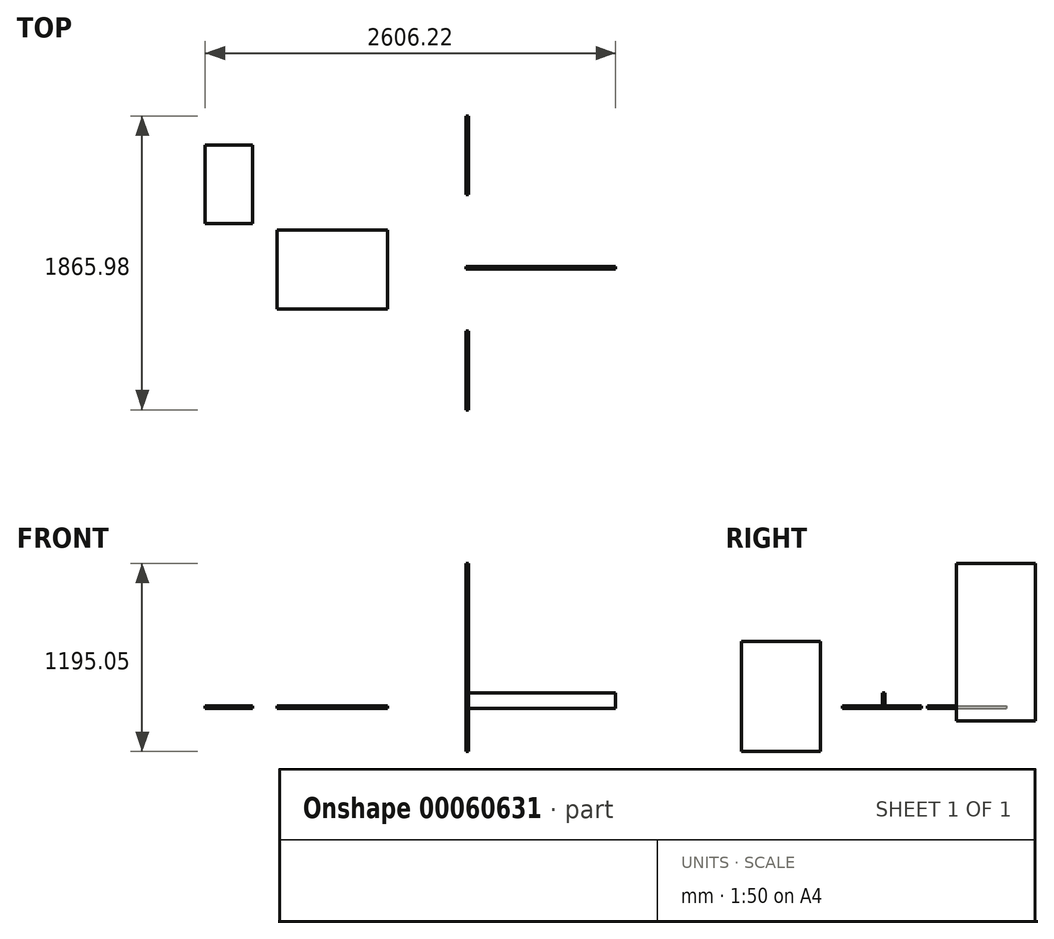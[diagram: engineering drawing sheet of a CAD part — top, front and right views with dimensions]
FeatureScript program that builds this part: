
annotation { "Feature Type Name" : "Feature", "Feature Type Description" : "" }
export const myFeature = defineFeature(function(context is Context, id is Id, definition is map)
    precondition{}
    {
        {
            var Q0;
            Q0=qCreatedBy(makeId("Front.planeOp"),FACE);
            var sketch = newSketch(context, id + "F0", { "sketchPlane" : qUnion([Q0])});
            skLineSegment(sketch, "E0.bottom", {"start": v(0, 100) * mm, "end": v(950, 100) * mm});
            skLineSegment(sketch, "E0.top", {"start": v(0, 0) * mm, "end": v(950, 0) * mm});
            skLineSegment(sketch, "E0.left", {"start": v(0, 100) * mm, "end": v(0, 0) * mm});
            skLineSegment(sketch, "E0.right", {"start": v(950, 100) * mm, "end": v(950, 0) * mm});
            skSolve(sketch);
        }
        {
            var Q0;
            Q0 = qSketchRegion(id + "F0", true);
            extrude(context, id + "F1", {"entities" : qUnion([Q0]), "depth" : 16 * mm});
        }
        {
            var Q0;
            Q0=qCreatedBy(makeId("Right.planeOp"),FACE);
            var sketch = newSketch(context, id + "F2", { "sketchPlane" : qUnion([Q0])});
            skLineSegment(sketch, "E1.bottom", {"start": v(-910.39, 426.54) * mm, "end": v(-410.39, 426.54) * mm});
            skLineSegment(sketch, "E1.top", {"start": v(-910.39, -273.46) * mm, "end": v(-410.39, -273.46) * mm});
            skLineSegment(sketch, "E1.left", {"start": v(-910.39, 426.54) * mm, "end": v(-910.39, -273.46) * mm});
            skLineSegment(sketch, "E1.right", {"start": v(-410.39, 426.54) * mm, "end": v(-410.39, -273.46) * mm});
            skSolve(sketch);
        }
        {
            var Q0;
            Q0 = qSketchRegion(id + "F2", true);
            extrude(context, id + "F3", {"entities" : qUnion([Q0]), "depth" : 16 * mm});
        }
        {
            var Q0;
            Q0=qCreatedBy(makeId("Right.planeOp"),FACE);
            var sketch = newSketch(context, id + "F4", { "sketchPlane" : qUnion([Q0])});
            skLineSegment(sketch, "E2.bottom", {"start": v(455.59, 921.6) * mm, "end": v(955.59, 921.6) * mm});
            skLineSegment(sketch, "E2.top", {"start": v(455.59, -78.4) * mm, "end": v(955.59, -78.4) * mm});
            skLineSegment(sketch, "E2.left", {"start": v(455.59, 921.6) * mm, "end": v(455.59, -78.4) * mm});
            skLineSegment(sketch, "E2.right", {"start": v(955.59, 921.6) * mm, "end": v(955.59, -78.4) * mm});
            skSolve(sketch);
        }
        {
            var Q0;
            Q0 = qSketchRegion(id + "F4", true);
            extrude(context, id + "F5", {"entities" : qUnion([Q0]), "depth" : 16 * mm});
        }
        {
            var Q0;
            Q0=qCreatedBy(makeId("Top.planeOp"),FACE);
            var sketch = newSketch(context, id + "F6", { "sketchPlane" : qUnion([Q0])});
            skLineSegment(sketch, "E3.bottom", {"start": v(-1200, -269.33) * mm, "end": v(-500, -269.33) * mm});
            skLineSegment(sketch, "E3.top", {"start": v(-1200, 230.67) * mm, "end": v(-500, 230.67) * mm});
            skLineSegment(sketch, "E3.left", {"start": v(-1200, -269.33) * mm, "end": v(-1200, 230.67) * mm});
            skLineSegment(sketch, "E3.right", {"start": v(-500, -269.33) * mm, "end": v(-500, 230.67) * mm});
            skSolve(sketch);
        }
        {
            var Q0;
            Q0 = qSketchRegion(id + "F6", true);
            extrude(context, id + "F7", {"entities" : qUnion([Q0]), "depth" : 16 * mm});
        }
        {
            var Q0;
            Q0=qCreatedBy(makeId("Top.planeOp"),FACE);
            var sketch = newSketch(context, id + "F8", { "sketchPlane" : qUnion([Q0])});
            skLineSegment(sketch, "E4.bottom", {"start": v(-1656.22, 271.51) * mm, "end": v(-1356.22, 271.51) * mm});
            skLineSegment(sketch, "E4.top", {"start": v(-1656.22, 771.51) * mm, "end": v(-1356.22, 771.51) * mm});
            skLineSegment(sketch, "E4.left", {"start": v(-1656.22, 271.51) * mm, "end": v(-1656.22, 771.51) * mm});
            skLineSegment(sketch, "E4.right", {"start": v(-1356.22, 271.51) * mm, "end": v(-1356.22, 771.51) * mm});
            skSolve(sketch);
        }
        {
            var Q0;
            Q0 = qSketchRegion(id + "F8", true);
            extrude(context, id + "F9", {"entities" : qUnion([Q0]), "depth" : 16 * mm});
        }
    });
